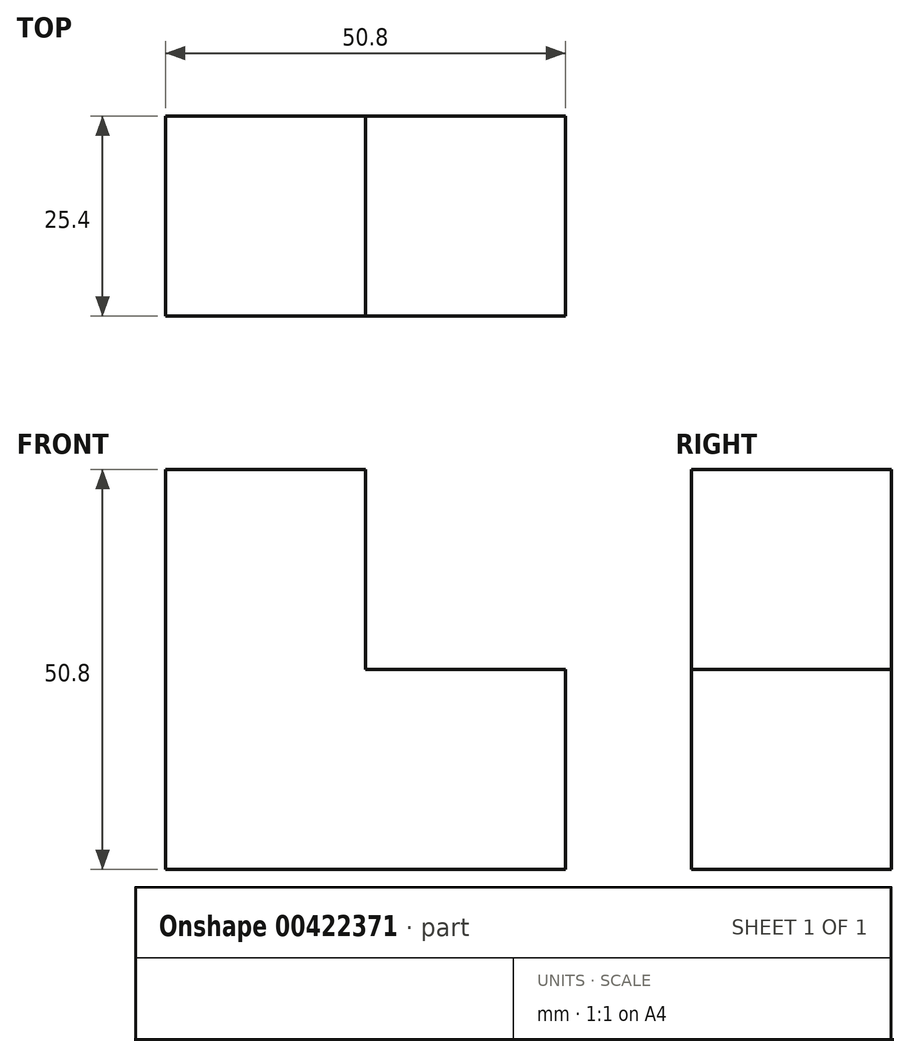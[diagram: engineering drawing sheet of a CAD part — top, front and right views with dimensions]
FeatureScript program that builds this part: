
annotation { "Feature Type Name" : "Feature", "Feature Type Description" : "" }
export const myFeature = defineFeature(function(context is Context, id is Id, definition is map)
    precondition{}
    {
        {
            var Q0;
            Q0=qCreatedBy(makeId("Front.planeOp"),FACE);
            var sketch = newSketch(context, id + "F0", { "sketchPlane" : qUnion([Q0])});
            skLineSegment(sketch, "E0", {"start": v(-46.52, -0.56) * mm, "end": v(-46.52, -51.36) * mm});
            skLineSegment(sketch, "E1", {"start": v(-46.52, -51.36) * mm, "end": v(4.28, -51.36) * mm});
            skLineSegment(sketch, "E2", {"start": v(-46.52, -0.56) * mm, "end": v(-21.12, -0.56) * mm});
            skLineSegment(sketch, "E3", {"start": v(-21.12, -0.56) * mm, "end": v(-21.12, -25.96) * mm});
            skLineSegment(sketch, "E4", {"start": v(-21.12, -25.96) * mm, "end": v(4.28, -25.96) * mm});
            skLineSegment(sketch, "E5", {"start": v(4.28, -25.96) * mm, "end": v(4.28, -51.36) * mm});
            skSolve(sketch);
        }
        {
            var Q0;
            Q0 = qSketchRegion(id + "F0", true);
            extrude(context, id + "F1", {"entities" : qUnion([Q0]), "depth" : 25.4 * mm});
        }
    });
